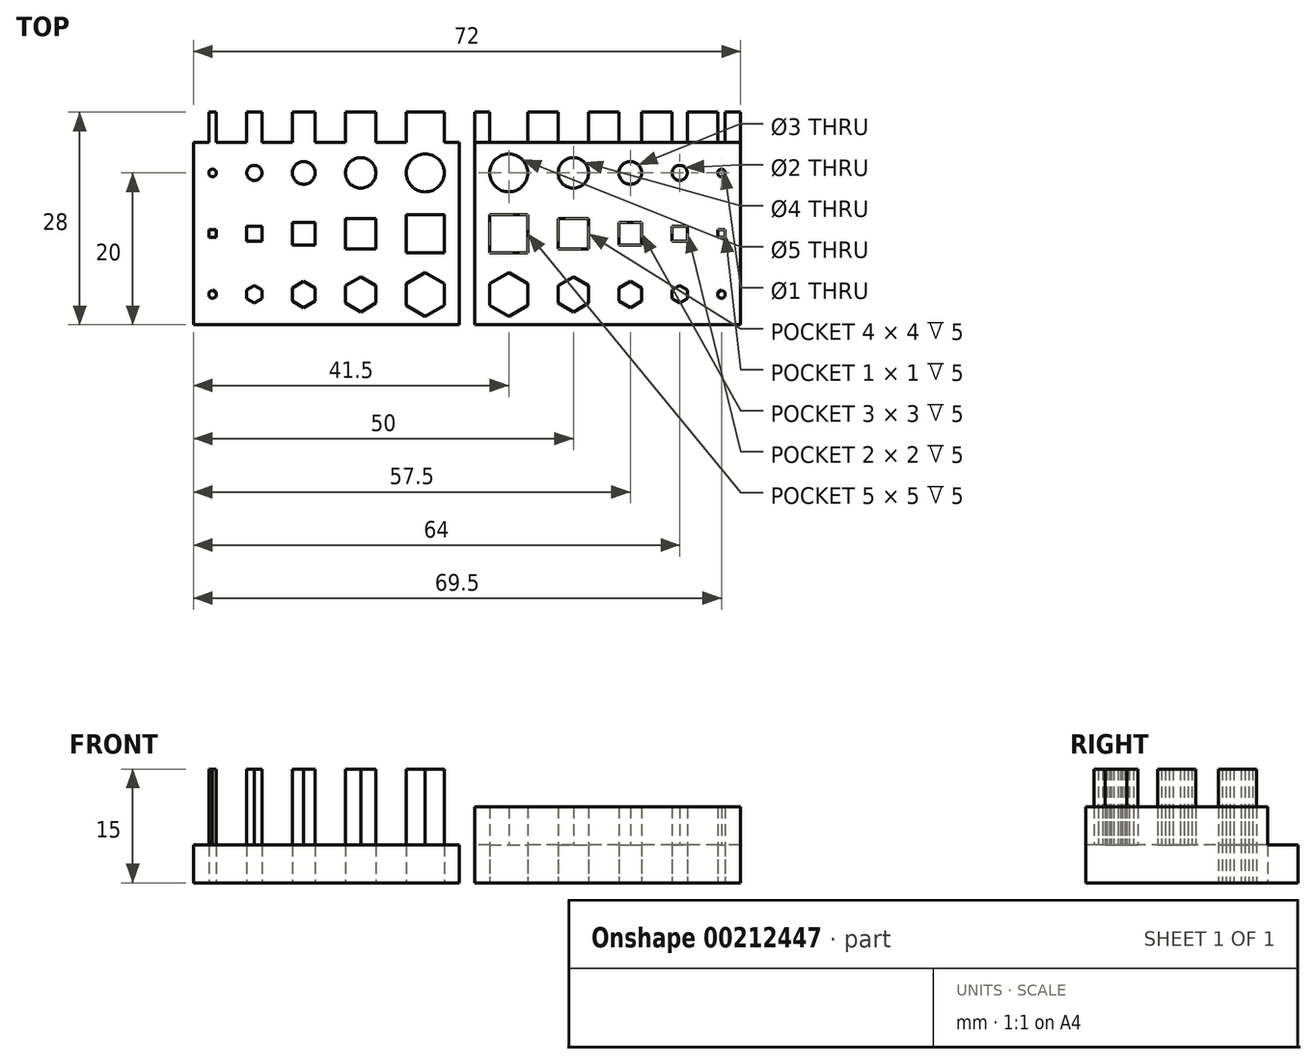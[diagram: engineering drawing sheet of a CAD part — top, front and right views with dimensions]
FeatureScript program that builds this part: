
annotation { "Feature Type Name" : "Feature", "Feature Type Description" : "" }
export const myFeature = defineFeature(function(context is Context, id is Id, definition is map)
    precondition{}
    {
        {
            var Q0;
            Q0=qCreatedBy(makeId("Top.planeOp"),FACE);
            var sketch = newSketch(context, id + "F0", { "sketchPlane" : qUnion([Q0])});
            skLineSegment(sketch, "E0.bottom", {"start": v(-36, 12) * mm, "end": v(36, 12) * mm});
            skLineSegment(sketch, "E0.top", {"start": v(-36, -12) * mm, "end": v(36, -12) * mm});
            skLineSegment(sketch, "E0.left", {"start": v(-36, 12) * mm, "end": v(-36, -12) * mm});
            skLineSegment(sketch, "E0.right", {"start": v(36, 12) * mm, "end": v(36, -12) * mm});
            skLineSegment(sketch, "E1", {"start": v(-36, 0) * mm, "end": v(36, 0) * mm, "construction": true});
            skLineSegment(sketch, "E2", {"start": v(-36, 8) * mm, "end": v(36, 8) * mm, "construction": true});
            skCircle(sketch, "E3", {"center": v(-33.5, 8) * mm, "radius": 0.5 * mm});
            skCircle(sketch, "E4", {"center": v(-28, 8) * mm, "radius": 1 * mm});
            skCircle(sketch, "E5", {"center": v(-21.5, 8) * mm, "radius": 1.5 * mm});
            skCircle(sketch, "E6", {"center": v(-14, 8) * mm, "radius": 2 * mm});
            skCircle(sketch, "E7", {"center": v(-5.5, 8) * mm, "radius": 2.5 * mm});
            skLineSegment(sketch, "E8.bottom", {"start": v(-34, 0.5) * mm, "end": v(-33, 0.5) * mm});
            skLineSegment(sketch, "E8.top", {"start": v(-34, -0.5) * mm, "end": v(-33, -0.5) * mm});
            skLineSegment(sketch, "E8.left", {"start": v(-34, 0.5) * mm, "end": v(-34, -0.5) * mm});
            skLineSegment(sketch, "E8.right", {"start": v(-33, 0.5) * mm, "end": v(-33, -0.5) * mm});
            skLineSegment(sketch, "E9.bottom", {"start": v(-23, 1.5) * mm, "end": v(-20, 1.5) * mm});
            skLineSegment(sketch, "E9.top", {"start": v(-23, -1.5) * mm, "end": v(-20, -1.5) * mm});
            skLineSegment(sketch, "E9.left", {"start": v(-23, 1.5) * mm, "end": v(-23, -1.5) * mm});
            skLineSegment(sketch, "E9.right", {"start": v(-20, 1.5) * mm, "end": v(-20, -1.5) * mm});
            skLineSegment(sketch, "E10.bottom", {"start": v(-16, 2) * mm, "end": v(-12, 2) * mm});
            skLineSegment(sketch, "E10.top", {"start": v(-16, -2) * mm, "end": v(-12, -2) * mm});
            skLineSegment(sketch, "E10.left", {"start": v(-16, 2) * mm, "end": v(-16, -2) * mm});
            skLineSegment(sketch, "E10.right", {"start": v(-12, 2) * mm, "end": v(-12, -2) * mm});
            skLineSegment(sketch, "E11.bottom", {"start": v(-8, 2.5) * mm, "end": v(-3, 2.5) * mm});
            skLineSegment(sketch, "E11.top", {"start": v(-8, -2.5) * mm, "end": v(-3, -2.5) * mm});
            skLineSegment(sketch, "E11.left", {"start": v(-8, 2.5) * mm, "end": v(-8, -2.5) * mm});
            skLineSegment(sketch, "E11.right", {"start": v(-3, 2.5) * mm, "end": v(-3, -2.5) * mm});
            skLineSegment(sketch, "E12", {"start": v(-8, 2.5) * mm, "end": v(-3, -2.5) * mm, "construction": true});
            skLineSegment(sketch, "E13", {"start": v(-16, 2) * mm, "end": v(-12, -2) * mm, "construction": true});
            skLineSegment(sketch, "E14", {"start": v(-23, 1.5) * mm, "end": v(-20, -1.5) * mm, "construction": true});
            skLineSegment(sketch, "E15", {"start": v(-34, 0.5) * mm, "end": v(-33, -0.5) * mm, "construction": true});
            skLineSegment(sketch, "E16.bottom", {"start": v(-29, 1) * mm, "end": v(-27, 1) * mm});
            skLineSegment(sketch, "E16.top", {"start": v(-29, -1) * mm, "end": v(-27, -1) * mm});
            skLineSegment(sketch, "E16.left", {"start": v(-29, 1) * mm, "end": v(-29, -1) * mm});
            skLineSegment(sketch, "E16.right", {"start": v(-27, 1) * mm, "end": v(-27, -1) * mm});
            skLineSegment(sketch, "E17.MirrorCS", {"start": v(-36, -8) * mm, "end": v(36, -8) * mm, "construction": true});
            skCircle(sketch, "E18.cCircle", {"center": v(-33.5, -8) * mm, "radius": 0.5 * mm, "construction": true});
            skLineSegment(sketch, "E18.0", {"start": v(-33.5, -7.42) * mm, "end": v(-33, -7.71) * mm});
            skLineSegment(sketch, "E18.1", {"start": v(-33, -7.71) * mm, "end": v(-33, -8.29) * mm});
            skLineSegment(sketch, "E18.2", {"start": v(-33, -8.29) * mm, "end": v(-33.5, -8.58) * mm});
            skLineSegment(sketch, "E18.3", {"start": v(-33.5, -8.58) * mm, "end": v(-34, -8.29) * mm});
            skLineSegment(sketch, "E18.4", {"start": v(-34, -8.29) * mm, "end": v(-34, -7.71) * mm});
            skLineSegment(sketch, "E18.5", {"start": v(-34, -7.71) * mm, "end": v(-33.5, -7.42) * mm});
            skPoint(sketch, "E18.0.midPoint", {"position": v(-33.25, -7.57) * mm});
            skCircle(sketch, "E19.cCircle", {"center": v(-21.5, -8) * mm, "radius": 1.5 * mm, "construction": true});
            skLineSegment(sketch, "E19.0", {"start": v(-21.5, -6.27) * mm, "end": v(-20, -7.13) * mm});
            skLineSegment(sketch, "E19.1", {"start": v(-20, -7.13) * mm, "end": v(-20, -8.87) * mm});
            skLineSegment(sketch, "E19.2", {"start": v(-20, -8.87) * mm, "end": v(-21.5, -9.73) * mm});
            skLineSegment(sketch, "E19.3", {"start": v(-21.5, -9.73) * mm, "end": v(-23, -8.87) * mm});
            skLineSegment(sketch, "E19.4", {"start": v(-23, -8.87) * mm, "end": v(-23, -7.13) * mm});
            skLineSegment(sketch, "E19.5", {"start": v(-23, -7.13) * mm, "end": v(-21.5, -6.27) * mm});
            skPoint(sketch, "E19.0.midPoint", {"position": v(-20.75, -6.7) * mm});
            skCircle(sketch, "E20.cCircle", {"center": v(-14, -8) * mm, "radius": 2 * mm, "construction": true});
            skLineSegment(sketch, "E20.0", {"start": v(-14, -5.7) * mm, "end": v(-12, -6.85) * mm});
            skLineSegment(sketch, "E20.1", {"start": v(-12, -6.85) * mm, "end": v(-12, -9.15) * mm});
            skLineSegment(sketch, "E20.2", {"start": v(-12, -9.15) * mm, "end": v(-14, -10.3) * mm});
            skLineSegment(sketch, "E20.3", {"start": v(-14, -10.3) * mm, "end": v(-16, -9.15) * mm});
            skLineSegment(sketch, "E20.4", {"start": v(-16, -9.15) * mm, "end": v(-16, -6.85) * mm});
            skLineSegment(sketch, "E20.5", {"start": v(-16, -6.85) * mm, "end": v(-14, -5.7) * mm});
            skPoint(sketch, "E20.0.midPoint", {"position": v(-13, -6.27) * mm});
            skCircle(sketch, "E21.cCircle", {"center": v(-5.5, -8) * mm, "radius": 2.5 * mm, "construction": true});
            skLineSegment(sketch, "E21.0", {"start": v(-8, -6.56) * mm, "end": v(-5.5, -5.11) * mm});
            skLineSegment(sketch, "E21.1", {"start": v(-5.5, -5.11) * mm, "end": v(-3, -6.56) * mm});
            skLineSegment(sketch, "E21.2", {"start": v(-3, -6.56) * mm, "end": v(-3, -9.44) * mm});
            skLineSegment(sketch, "E21.3", {"start": v(-3, -9.44) * mm, "end": v(-5.5, -10.89) * mm});
            skLineSegment(sketch, "E21.4", {"start": v(-5.5, -10.89) * mm, "end": v(-8, -9.44) * mm});
            skLineSegment(sketch, "E21.5", {"start": v(-8, -9.44) * mm, "end": v(-8, -6.56) * mm});
            skPoint(sketch, "E21.0.midPoint", {"position": v(-6.75, -5.83) * mm});
            skCircle(sketch, "E22.cCircle", {"center": v(-28, -8) * mm, "radius": 1 * mm, "construction": true});
            skLineSegment(sketch, "E22.0", {"start": v(-28, -6.85) * mm, "end": v(-27, -7.42) * mm});
            skLineSegment(sketch, "E22.1", {"start": v(-27, -7.42) * mm, "end": v(-27, -8.58) * mm});
            skLineSegment(sketch, "E22.2", {"start": v(-27, -8.58) * mm, "end": v(-28, -9.15) * mm});
            skLineSegment(sketch, "E22.3", {"start": v(-28, -9.15) * mm, "end": v(-29, -8.58) * mm});
            skLineSegment(sketch, "E22.4", {"start": v(-29, -8.58) * mm, "end": v(-29, -7.42) * mm});
            skLineSegment(sketch, "E22.5", {"start": v(-29, -7.42) * mm, "end": v(-28, -6.85) * mm});
            skPoint(sketch, "E22.0.midPoint", {"position": v(-27.5, -7.13) * mm});
            skLineSegment(sketch, "E23.MirrorCS", {"start": v(33, -7.71) * mm, "end": v(33, -8.29) * mm});
            skLineSegment(sketch, "E24.MirrorCS", {"start": v(33.5, -7.42) * mm, "end": v(33, -7.71) * mm});
            skLineSegment(sketch, "E25.MirrorCS", {"start": v(33.5, -8.58) * mm, "end": v(34, -8.29) * mm});
            skLineSegment(sketch, "E26.MirrorCS", {"start": v(33, -8.29) * mm, "end": v(33.5, -8.58) * mm});
            skLineSegment(sketch, "E27.MirrorCS", {"start": v(27, -8.58) * mm, "end": v(28, -9.15) * mm});
            skLineSegment(sketch, "E28.MirrorCS", {"start": v(34, -7.71) * mm, "end": v(33.5, -7.42) * mm});
            skLineSegment(sketch, "E29.MirrorCS", {"start": v(34, 0.5) * mm, "end": v(33, -0.5) * mm, "construction": true});
            skCircle(sketch, "E30.MirrorC", {"center": v(33.5, -8) * mm, "radius": 0.5 * mm, "construction": true});
            skLineSegment(sketch, "E31.MirrorCS", {"start": v(34, -8.29) * mm, "end": v(34, -7.71) * mm});
            skLineSegment(sketch, "E32.MirrorCS", {"start": v(28, -9.15) * mm, "end": v(29, -8.58) * mm});
            skLineSegment(sketch, "E33.MirrorCS", {"start": v(34, 0.5) * mm, "end": v(33, 0.5) * mm});
            skLineSegment(sketch, "E34.MirrorCS", {"start": v(20, -7.13) * mm, "end": v(20, -8.87) * mm});
            skLineSegment(sketch, "E35.MirrorCS", {"start": v(21.5, -6.27) * mm, "end": v(20, -7.13) * mm});
            skLineSegment(sketch, "E36.MirrorCS", {"start": v(20, -8.87) * mm, "end": v(21.5, -9.73) * mm});
            skLineSegment(sketch, "E37.MirrorCS", {"start": v(34, 0.5) * mm, "end": v(34, -0.5) * mm});
            skLineSegment(sketch, "E38.MirrorCS", {"start": v(21.5, -9.73) * mm, "end": v(23, -8.87) * mm});
            skLineSegment(sketch, "E39.MirrorCS", {"start": v(29, -7.42) * mm, "end": v(28, -6.85) * mm});
            skCircle(sketch, "E40.MirrorC", {"center": v(21.5, -8) * mm, "radius": 1.5 * mm, "construction": true});
            skLineSegment(sketch, "E41.MirrorCS", {"start": v(28, -6.85) * mm, "end": v(27, -7.42) * mm});
            skLineSegment(sketch, "E42.MirrorCS", {"start": v(23, -7.13) * mm, "end": v(21.5, -6.27) * mm});
            skLineSegment(sketch, "E43.MirrorCS", {"start": v(33, 0.5) * mm, "end": v(33, -0.5) * mm});
            skLineSegment(sketch, "E44.MirrorCS", {"start": v(29, -8.58) * mm, "end": v(29, -7.42) * mm});
            skLineSegment(sketch, "E45.MirrorCS", {"start": v(23, -8.87) * mm, "end": v(23, -7.13) * mm});
            skLineSegment(sketch, "E46.MirrorCS", {"start": v(34, -0.5) * mm, "end": v(33, -0.5) * mm});
            skCircle(sketch, "E47.MirrorC", {"center": v(28, -8) * mm, "radius": 1 * mm, "construction": true});
            skLineSegment(sketch, "E48.MirrorCS", {"start": v(27, -7.42) * mm, "end": v(27, -8.58) * mm});
            skLineSegment(sketch, "E49.MirrorCS", {"start": v(16, -9.15) * mm, "end": v(16, -6.85) * mm});
            skCircle(sketch, "E50.MirrorC", {"center": v(33.5, 8) * mm, "radius": 0.5 * mm});
            skLineSegment(sketch, "E51.MirrorCS", {"start": v(8, -6.56) * mm, "end": v(5.5, -5.11) * mm});
            skLineSegment(sketch, "E52.MirrorCS", {"start": v(3, -9.44) * mm, "end": v(5.5, -10.89) * mm});
            skLineSegment(sketch, "E53.MirrorCS", {"start": v(3, -6.56) * mm, "end": v(3, -9.44) * mm});
            skLineSegment(sketch, "E54.MirrorCS", {"start": v(14, -10.3) * mm, "end": v(16, -9.15) * mm});
            skLineSegment(sketch, "E55.MirrorCS", {"start": v(16, -6.85) * mm, "end": v(14, -5.7) * mm});
            skLineSegment(sketch, "E56.MirrorCS", {"start": v(12, -6.85) * mm, "end": v(12, -9.15) * mm});
            skLineSegment(sketch, "E57.MirrorCS", {"start": v(14, -5.7) * mm, "end": v(12, -6.85) * mm});
            skPoint(sketch, "E58.MirrorP", {"position": v(13, -6.27) * mm});
            skLineSegment(sketch, "E59.MirrorCS", {"start": v(20, 1.5) * mm, "end": v(20, -1.5) * mm});
            skPoint(sketch, "E60.MirrorP", {"position": v(27.5, -7.13) * mm});
            skLineSegment(sketch, "E61.MirrorCS", {"start": v(16, -2) * mm, "end": v(12, -2) * mm});
            skLineSegment(sketch, "E62.MirrorCS", {"start": v(8, 2.5) * mm, "end": v(3, -2.5) * mm, "construction": true});
            skLineSegment(sketch, "E63.MirrorCS", {"start": v(8, 2.5) * mm, "end": v(3, 2.5) * mm});
            skCircle(sketch, "E64.MirrorC", {"center": v(21.5, 8) * mm, "radius": 1.5 * mm});
            skCircle(sketch, "E65.MirrorC", {"center": v(28, 8) * mm, "radius": 1 * mm});
            skLineSegment(sketch, "E66.MirrorCS", {"start": v(16, 2) * mm, "end": v(16, -2) * mm});
            skLineSegment(sketch, "E67.MirrorCS", {"start": v(16, 2) * mm, "end": v(12, -2) * mm, "construction": true});
            skPoint(sketch, "E68.MirrorP", {"position": v(33.25, -7.57) * mm});
            skCircle(sketch, "E69.MirrorC", {"center": v(14, 8) * mm, "radius": 2 * mm});
            skCircle(sketch, "E70.MirrorC", {"center": v(5.5, 8) * mm, "radius": 2.5 * mm});
            skLineSegment(sketch, "E71.MirrorCS", {"start": v(23, -1.5) * mm, "end": v(20, -1.5) * mm});
            skLineSegment(sketch, "E72.MirrorCS", {"start": v(12, -9.15) * mm, "end": v(14, -10.3) * mm});
            skPoint(sketch, "E73.MirrorP", {"position": v(20.75, -6.7) * mm});
            skLineSegment(sketch, "E74.MirrorCS", {"start": v(29, 1) * mm, "end": v(27, 1) * mm});
            skCircle(sketch, "E75.MirrorC", {"center": v(14, -8) * mm, "radius": 2 * mm, "construction": true});
            skLineSegment(sketch, "E76.MirrorCS", {"start": v(8, -9.44) * mm, "end": v(8, -6.56) * mm});
            skLineSegment(sketch, "E77.MirrorCS", {"start": v(12, 2) * mm, "end": v(12, -2) * mm});
            skLineSegment(sketch, "E78.MirrorCS", {"start": v(23, 1.5) * mm, "end": v(20, 1.5) * mm});
            skCircle(sketch, "E79.MirrorC", {"center": v(5.5, -8) * mm, "radius": 2.5 * mm, "construction": true});
            skLineSegment(sketch, "E80.MirrorCS", {"start": v(23, 1.5) * mm, "end": v(20, -1.5) * mm, "construction": true});
            skLineSegment(sketch, "E81.MirrorCS", {"start": v(29, -1) * mm, "end": v(27, -1) * mm});
            skLineSegment(sketch, "E82.MirrorCS", {"start": v(3, 2.5) * mm, "end": v(3, -2.5) * mm});
            skLineSegment(sketch, "E83.MirrorCS", {"start": v(27, 1) * mm, "end": v(27, -1) * mm});
            skLineSegment(sketch, "E84.MirrorCS", {"start": v(23, 1.5) * mm, "end": v(23, -1.5) * mm});
            skPoint(sketch, "E85.MirrorP", {"position": v(6.75, -5.83) * mm});
            skLineSegment(sketch, "E86.MirrorCS", {"start": v(8, 2.5) * mm, "end": v(8, -2.5) * mm});
            skLineSegment(sketch, "E87.MirrorCS", {"start": v(16, 2) * mm, "end": v(12, 2) * mm});
            skLineSegment(sketch, "E88.MirrorCS", {"start": v(5.5, -5.11) * mm, "end": v(3, -6.56) * mm});
            skLineSegment(sketch, "E89.MirrorCS", {"start": v(29, 1) * mm, "end": v(29, -1) * mm});
            skLineSegment(sketch, "E90.MirrorCS", {"start": v(5.5, -10.89) * mm, "end": v(8, -9.44) * mm});
            skLineSegment(sketch, "E91.MirrorCS", {"start": v(8, -2.5) * mm, "end": v(3, -2.5) * mm});
            skLineSegment(sketch, "E92.bottom", {"start": v(-34, 16) * mm, "end": v(-33, 16) * mm});
            skLineSegment(sketch, "E92.top", {"start": v(-34, 12) * mm, "end": v(-33, 12) * mm});
            skLineSegment(sketch, "E92.left", {"start": v(-34, 16) * mm, "end": v(-34, 12) * mm});
            skLineSegment(sketch, "E92.right", {"start": v(-33, 16) * mm, "end": v(-33, 12) * mm});
            skLineSegment(sketch, "E93.bottom", {"start": v(-29, 16) * mm, "end": v(-27, 16) * mm});
            skLineSegment(sketch, "E93.top", {"start": v(-29, 12) * mm, "end": v(-27, 12) * mm});
            skLineSegment(sketch, "E93.left", {"start": v(-29, 16) * mm, "end": v(-29, 12) * mm});
            skLineSegment(sketch, "E93.right", {"start": v(-27, 16) * mm, "end": v(-27, 12) * mm});
            skLineSegment(sketch, "E94.bottom", {"start": v(-23, 16) * mm, "end": v(-20, 16) * mm});
            skLineSegment(sketch, "E94.top", {"start": v(-23, 12) * mm, "end": v(-20, 12) * mm});
            skLineSegment(sketch, "E94.left", {"start": v(-23, 16) * mm, "end": v(-23, 12) * mm});
            skLineSegment(sketch, "E94.right", {"start": v(-20, 16) * mm, "end": v(-20, 12) * mm});
            skLineSegment(sketch, "E95.bottom", {"start": v(-16, 16) * mm, "end": v(-12, 16) * mm});
            skLineSegment(sketch, "E95.top", {"start": v(-16, 12) * mm, "end": v(-12, 12) * mm});
            skLineSegment(sketch, "E95.left", {"start": v(-16, 16) * mm, "end": v(-16, 12) * mm});
            skLineSegment(sketch, "E95.right", {"start": v(-12, 16) * mm, "end": v(-12, 12) * mm});
            skLineSegment(sketch, "E96.bottom", {"start": v(-8, 16) * mm, "end": v(-3, 16) * mm});
            skLineSegment(sketch, "E96.top", {"start": v(-8, 12) * mm, "end": v(-3, 12) * mm});
            skLineSegment(sketch, "E96.left", {"start": v(-8, 16) * mm, "end": v(-8, 12) * mm});
            skLineSegment(sketch, "E96.right", {"start": v(-3, 16) * mm, "end": v(-3, 12) * mm});
            skLineSegment(sketch, "E97.MirrorCS", {"start": v(34, 16) * mm, "end": v(33, 16) * mm});
            skLineSegment(sketch, "E98.MirrorCS", {"start": v(34, 12) * mm, "end": v(33, 12) * mm});
            skLineSegment(sketch, "E99.MirrorCS", {"start": v(29, 12) * mm, "end": v(27, 12) * mm});
            skLineSegment(sketch, "E100.MirrorCS", {"start": v(29, 16) * mm, "end": v(27, 16) * mm});
            skLineSegment(sketch, "E101.MirrorCS", {"start": v(16, 16) * mm, "end": v(16, 12) * mm});
            skLineSegment(sketch, "E102.MirrorCS", {"start": v(8, 16) * mm, "end": v(8, 12) * mm});
            skLineSegment(sketch, "E103.MirrorCS", {"start": v(20, 16) * mm, "end": v(20, 12) * mm});
            skLineSegment(sketch, "E104.MirrorCS", {"start": v(16, 16) * mm, "end": v(12, 16) * mm});
            skLineSegment(sketch, "E105.MirrorCS", {"start": v(23, 16) * mm, "end": v(23, 12) * mm});
            skLineSegment(sketch, "E106.MirrorCS", {"start": v(16, 12) * mm, "end": v(12, 12) * mm});
            skLineSegment(sketch, "E107.MirrorCS", {"start": v(12, 16) * mm, "end": v(12, 12) * mm});
            skLineSegment(sketch, "E108.MirrorCS", {"start": v(8, 16) * mm, "end": v(3, 16) * mm});
            skLineSegment(sketch, "E109.MirrorCS", {"start": v(8, 12) * mm, "end": v(3, 12) * mm});
            skLineSegment(sketch, "E110.MirrorCS", {"start": v(34, 16) * mm, "end": v(34, 12) * mm});
            skLineSegment(sketch, "E111.MirrorCS", {"start": v(23, 16) * mm, "end": v(20, 16) * mm});
            skLineSegment(sketch, "E112.MirrorCS", {"start": v(23, 12) * mm, "end": v(20, 12) * mm});
            skLineSegment(sketch, "E113.MirrorCS", {"start": v(33, 16) * mm, "end": v(33, 12) * mm});
            skLineSegment(sketch, "E114.MirrorCS", {"start": v(29, 16) * mm, "end": v(29, 12) * mm});
            skLineSegment(sketch, "E115.MirrorCS", {"start": v(3, 16) * mm, "end": v(3, 12) * mm});
            skLineSegment(sketch, "E116.MirrorCS", {"start": v(27, 16) * mm, "end": v(27, 12) * mm});
            skLineSegment(sketch, "E117.bottom", {"start": v(36, 12) * mm, "end": v(0, 12) * mm});
            skLineSegment(sketch, "E117.top", {"start": v(36, 16) * mm, "end": v(0, 16) * mm});
            skLineSegment(sketch, "E117.left", {"start": v(36, 12) * mm, "end": v(36, 16) * mm});
            skLineSegment(sketch, "E117.right", {"start": v(0, 12) * mm, "end": v(0, 16) * mm});
            skLineSegment(sketch, "E118.1.18", {"start": v(36, -12.69) * mm, "end": v(-36, -12.69) * mm});
            skPoint(sketch, "E118.center", {"position": v(0, -0.34) * mm});
            skLineSegment(sketch, "E119", {"start": v(0, 12) * mm, "end": v(0, -12.69) * mm});
            skLineSegment(sketch, "E120.bottom", {"start": v(-1, 18.91) * mm, "end": v(1, 18.91) * mm});
            skLineSegment(sketch, "E120.top", {"start": v(-1, -18.8) * mm, "end": v(1, -18.8) * mm});
            skLineSegment(sketch, "E120.left", {"start": v(-1, 18.91) * mm, "end": v(-1, -18.8) * mm});
            skLineSegment(sketch, "E120.right", {"start": v(1, 18.91) * mm, "end": v(1, -18.8) * mm});
            skSolve(sketch);
        }
        {
            var Q0;
            Q0=makeQuery(id+"F0.imprint","IMPRINT",FACE,{"disambiguationData":[TD([[makeQuery(id+"F0.imprint","IMPRINT",EDGE,{"derivedFrom":sQuery(id+"F0.wireOp",EDGE,"E96.bottom")}),-1.0]])]});
            var Q1;
            Q1=makeQuery(id+"F0.imprint","IMPRINT",FACE,{"disambiguationData":[TD([[makeQuery(id+"F0.imprint","IMPRINT",EDGE,{"derivedFrom":sQuery(id+"F0.wireOp",EDGE,"E95.bottom")}),-1.0]])]});
            var Q2;
            Q2=makeQuery(id+"F0.imprint","IMPRINT",FACE,{"disambiguationData":[TD([[makeQuery(id+"F0.imprint","IMPRINT",EDGE,{"derivedFrom":sQuery(id+"F0.wireOp",EDGE,"E93.bottom")}),-1.0]])]});
            var Q3;
            Q3=makeQuery(id+"F0.imprint","IMPRINT",FACE,{"disambiguationData":[TD([[makeQuery(id+"F0.imprint","IMPRINT",EDGE,{"derivedFrom":sQuery(id+"F0.wireOp",EDGE,"E94.bottom")}),-1.0]])]});
            var Q4;
            Q4=makeQuery(id+"F0.imprint","IMPRINT",FACE,{"disambiguationData":[TD([[makeQuery(id+"F0.imprint","IMPRINT",EDGE,{"derivedFrom":sQuery(id+"F0.wireOp",EDGE,"E92.bottom")}),-1.0]])]});
            var Q5;
            {var subQ4=sQuery(id+"F0.wireOp",EDGE,"E0.left");Q5=makeQuery(id+"F0.imprint","IMPRINT",FACE,{"disambiguationData":[TD([[makeQuery(id+"F0.imprint","IMPRINT",EDGE,{"derivedFrom":subQ4}),1.0]])]});}
            var Q6;
            Q6=makeQuery(id+"F0.imprint","IMPRINT",FACE,{"disambiguationData":[TD([[makeQuery(id+"F0.imprint","IMPRINT",EDGE,{"derivedFrom":sQuery(id+"F0.wireOp",EDGE,"E20.0")}),-1.0]])]});
            var Q7;
            Q7=makeQuery(id+"F0.imprint","IMPRINT",FACE,{"disambiguationData":[TD([[makeQuery(id+"F0.imprint","IMPRINT",EDGE,{"derivedFrom":sQuery(id+"F0.wireOp",EDGE,"E19.0")}),-1.0]])]});
            var Q8;
            Q8=makeQuery(id+"F0.imprint","IMPRINT",FACE,{"disambiguationData":[TD([[makeQuery(id+"F0.imprint","IMPRINT",EDGE,{"derivedFrom":sQuery(id+"F0.wireOp",EDGE,"E11.bottom")}),-1.0]])]});
            var Q9;
            Q9=makeQuery(id+"F0.imprint","IMPRINT",FACE,{"disambiguationData":[TD([[makeQuery(id+"F0.imprint","IMPRINT",EDGE,{"derivedFrom":sQuery(id+"F0.wireOp",EDGE,"E16.bottom")}),-1.0]])]});
            var Q10;
            Q10=makeQuery(id+"F0.imprint","IMPRINT",FACE,{"disambiguationData":[TD([[makeQuery(id+"F0.imprint","IMPRINT",EDGE,{"derivedFrom":sQuery(id+"F0.wireOp",EDGE,"E10.bottom")}),-1.0]])]});
            var Q11;
            Q11=makeQuery(id+"F0.imprint","IMPRINT",FACE,{"disambiguationData":[TD([[makeQuery(id+"F0.imprint","IMPRINT",EDGE,{"derivedFrom":sQuery(id+"F0.wireOp",EDGE,"E9.bottom")}),-1.0]])]});
            var Q12;
            Q12=makeQuery(id+"F0.imprint","IMPRINT",FACE,{"disambiguationData":[TD([[makeQuery(id+"F0.imprint","IMPRINT",EDGE,{"derivedFrom":sQuery(id+"F0.wireOp",EDGE,"E4")}),1.0]])]});
            var Q13;
            Q13=makeQuery(id+"F0.imprint","IMPRINT",FACE,{"disambiguationData":[TD([[makeQuery(id+"F0.imprint","IMPRINT",EDGE,{"derivedFrom":sQuery(id+"F0.wireOp",EDGE,"E22.0")}),-1.0]])]});
            var Q14;
            Q14=makeQuery(id+"F0.imprint","IMPRINT",FACE,{"disambiguationData":[TD([[makeQuery(id+"F0.imprint","IMPRINT",EDGE,{"derivedFrom":sQuery(id+"F0.wireOp",EDGE,"E3")}),1.0]])]});
            var Q15;
            Q15=makeQuery(id+"F0.imprint","IMPRINT",FACE,{"disambiguationData":[TD([[makeQuery(id+"F0.imprint","IMPRINT",EDGE,{"derivedFrom":sQuery(id+"F0.wireOp",EDGE,"E18.0")}),-1.0]])]});
            var Q16;
            Q16=makeQuery(id+"F0.imprint","IMPRINT",FACE,{"disambiguationData":[TD([[makeQuery(id+"F0.imprint","IMPRINT",EDGE,{"derivedFrom":sQuery(id+"F0.wireOp",EDGE,"E8.bottom")}),-1.0]])]});
            var Q17;
            Q17=makeQuery(id+"F0.imprint","IMPRINT",FACE,{"disambiguationData":[TD([[makeQuery(id+"F0.imprint","IMPRINT",EDGE,{"derivedFrom":sQuery(id+"F0.wireOp",EDGE,"E7")}),1.0]])]});
            var Q18;
            Q18=makeQuery(id+"F0.imprint","IMPRINT",FACE,{"disambiguationData":[TD([[makeQuery(id+"F0.imprint","IMPRINT",EDGE,{"derivedFrom":sQuery(id+"F0.wireOp",EDGE,"E6")}),1.0]])]});
            var Q19;
            Q19=makeQuery(id+"F0.imprint","IMPRINT",FACE,{"disambiguationData":[TD([[makeQuery(id+"F0.imprint","IMPRINT",EDGE,{"derivedFrom":sQuery(id+"F0.wireOp",EDGE,"E5")}),1.0]])]});
            var Q20;
            Q20=makeQuery(id+"F0.imprint","IMPRINT",FACE,{"disambiguationData":[TD([[makeQuery(id+"F0.imprint","IMPRINT",EDGE,{"derivedFrom":sQuery(id+"F0.wireOp",EDGE,"E21.0")}),-1.0]])]});
            var Q21;
            Q21=makeQuery(id+"F0.imprint","IMPRINT",FACE,{"disambiguationData":[TD([[makeQuery(id+"F0.imprint","IMPRINT",EDGE,{"derivedFrom":sQuery(id+"F0.wireOp",EDGE,"E51.MirrorCS")}),1.0]])]});
            var Q22;
            Q22=makeQuery(id+"F0.imprint","IMPRINT",FACE,{"disambiguationData":[TD([[makeQuery(id+"F0.imprint","IMPRINT",EDGE,{"derivedFrom":sQuery(id+"F0.wireOp",EDGE,"E63.MirrorCS")}),1.0]])]});
            var Q23;
            Q23=makeQuery(id+"F0.imprint","IMPRINT",FACE,{"disambiguationData":[TD([[makeQuery(id+"F0.imprint","IMPRINT",EDGE,{"derivedFrom":sQuery(id+"F0.wireOp",EDGE,"E70.MirrorC")}),-1.0]])]});
            var Q24;
            {var subQ0=sQuery(id+"F0.wireOp",EDGE,"E0.right");Q24=makeQuery(id+"F0.imprint","IMPRINT",FACE,{"disambiguationData":[TD([[makeQuery(id+"F0.imprint","IMPRINT",EDGE,{"derivedFrom":subQ0}),-1.0]])]});}
            var Q25;
            Q25=makeQuery(id+"F0.imprint","IMPRINT",FACE,{"disambiguationData":[TD([[makeQuery(id+"F0.imprint","IMPRINT",EDGE,{"derivedFrom":sQuery(id+"F0.wireOp",EDGE,"E59.MirrorCS")}),1.0]])]});
            var Q26;
            {var subQ0=sQuery(id+"F0.wireOp",EDGE,"E102.MirrorCS");Q26=makeQuery(id+"F0.imprint","IMPRINT",FACE,{"disambiguationData":[TD([[makeQuery(id+"F0.imprint","IMPRINT",EDGE,{"derivedFrom":subQ0}),1.0]])]});}
            var Q27;
            Q27=makeQuery(id+"F0.imprint","IMPRINT",FACE,{"disambiguationData":[TD([[makeQuery(id+"F0.imprint","IMPRINT",EDGE,{"derivedFrom":sQuery(id+"F0.wireOp",EDGE,"E61.MirrorCS")}),-1.0]])]});
            var Q28;
            {var subQ0=sQuery(id+"F0.wireOp",EDGE,"E105.MirrorCS");Q28=makeQuery(id+"F0.imprint","IMPRINT",FACE,{"disambiguationData":[TD([[makeQuery(id+"F0.imprint","IMPRINT",EDGE,{"derivedFrom":subQ0}),1.0]])]});}
            var Q29;
            Q29=makeQuery(id+"F0.imprint","IMPRINT",FACE,{"disambiguationData":[TD([[makeQuery(id+"F0.imprint","IMPRINT",EDGE,{"derivedFrom":sQuery(id+"F0.wireOp",EDGE,"E65.MirrorC")}),-1.0]])]});
            var Q30;
            Q30=makeQuery(id+"F0.imprint","IMPRINT",FACE,{"disambiguationData":[TD([[makeQuery(id+"F0.imprint","IMPRINT",EDGE,{"derivedFrom":sQuery(id+"F0.wireOp",EDGE,"E74.MirrorCS")}),1.0]])]});
            var Q31;
            Q31=makeQuery(id+"F0.imprint","IMPRINT",FACE,{"disambiguationData":[TD([[makeQuery(id+"F0.imprint","IMPRINT",EDGE,{"derivedFrom":sQuery(id+"F0.wireOp",EDGE,"E34.MirrorCS")}),1.0]])]});
            var Q32;
            {var subQ0=sQuery(id+"F0.wireOp",EDGE,"E113.MirrorCS");Q32=makeQuery(id+"F0.imprint","IMPRINT",FACE,{"disambiguationData":[TD([[makeQuery(id+"F0.imprint","IMPRINT",EDGE,{"derivedFrom":subQ0}),-1.0]])]});}
            var Q33;
            Q33=makeQuery(id+"F0.imprint","IMPRINT",FACE,{"disambiguationData":[TD([[makeQuery(id+"F0.imprint","IMPRINT",EDGE,{"derivedFrom":sQuery(id+"F0.wireOp",EDGE,"E49.MirrorCS")}),1.0]])]});
            var Q34;
            {var subQ0=sQuery(id+"F0.wireOp",EDGE,"E110.MirrorCS");Q34=makeQuery(id+"F0.imprint","IMPRINT",FACE,{"disambiguationData":[TD([[makeQuery(id+"F0.imprint","IMPRINT",EDGE,{"derivedFrom":subQ0}),1.0]])]});}
            var Q35;
            {var subQ0=sQuery(id+"F0.wireOp",EDGE,"E115.MirrorCS");Q35=makeQuery(id+"F0.imprint","IMPRINT",FACE,{"disambiguationData":[TD([[makeQuery(id+"F0.imprint","IMPRINT",EDGE,{"derivedFrom":subQ0}),-1.0]])]});}
            var Q36;
            Q36=makeQuery(id+"F0.imprint","IMPRINT",FACE,{"disambiguationData":[TD([[makeQuery(id+"F0.imprint","IMPRINT",EDGE,{"derivedFrom":sQuery(id+"F0.wireOp",EDGE,"E69.MirrorC")}),-1.0]])]});
            var Q37;
            {var subQ0=sQuery(id+"F0.wireOp",EDGE,"E101.MirrorCS");Q37=makeQuery(id+"F0.imprint","IMPRINT",FACE,{"disambiguationData":[TD([[makeQuery(id+"F0.imprint","IMPRINT",EDGE,{"derivedFrom":subQ0}),1.0]])]});}
            var Q38;
            Q38=makeQuery(id+"F0.imprint","IMPRINT",FACE,{"disambiguationData":[TD([[makeQuery(id+"F0.imprint","IMPRINT",EDGE,{"derivedFrom":sQuery(id+"F0.wireOp",EDGE,"E64.MirrorC")}),-1.0]])]});
            var Q39;
            Q39=makeQuery(id+"F0.imprint","IMPRINT",FACE,{"disambiguationData":[TD([[makeQuery(id+"F0.imprint","IMPRINT",EDGE,{"derivedFrom":sQuery(id+"F0.wireOp",EDGE,"E27.MirrorCS")}),1.0]])]});
            var Q40;
            Q40=makeQuery(id+"F0.imprint","IMPRINT",FACE,{"disambiguationData":[TD([[makeQuery(id+"F0.imprint","IMPRINT",EDGE,{"derivedFrom":sQuery(id+"F0.wireOp",EDGE,"E50.MirrorC")}),-1.0]])]});
            var Q41;
            Q41=makeQuery(id+"F0.imprint","IMPRINT",FACE,{"disambiguationData":[TD([[makeQuery(id+"F0.imprint","IMPRINT",EDGE,{"derivedFrom":sQuery(id+"F0.wireOp",EDGE,"E23.MirrorCS")}),1.0]])]});
            var Q42;
            Q42=makeQuery(id+"F0.imprint","IMPRINT",FACE,{"disambiguationData":[TD([[makeQuery(id+"F0.imprint","IMPRINT",EDGE,{"derivedFrom":sQuery(id+"F0.wireOp",EDGE,"E33.MirrorCS")}),1.0]])]});
            extrude(context, id + "F1", {"entities" : qUnion([Q0, Q1, Q2, Q3, Q4, Q5, Q6, Q7, Q8, Q9, Q10, Q11, Q12, Q13, Q14, Q15, Q16, Q17, Q18, Q19, Q20, Q21, Q22, Q23, Q24, Q25, Q26, Q27, Q28, Q29, Q30, Q31, Q32, Q33, Q34, Q35, Q36, Q37, Q38, Q39, Q40, Q41, Q42]), "depth" : 5 * mm});
        }
        {
            var Q0;
            {var subQ0=sQuery(id+"F0.wireOp",EDGE,"E0.right");Q0=makeQuery(id+"F0.imprint","IMPRINT",FACE,{"disambiguationData":[TD([[makeQuery(id+"F0.imprint","IMPRINT",EDGE,{"derivedFrom":subQ0}),-1.0]])]});}
            extrude(context, id + "F2", {"entities" : qUnion([Q0]), "operationType" : NewBodyOperationType.ADD, "depth" : 10 * mm});
        }
        {
            var Q0;
            Q0=makeQuery(id+"F0.imprint","IMPRINT",FACE,{"disambiguationData":[TD([[makeQuery(id+"F0.imprint","IMPRINT",EDGE,{"derivedFrom":sQuery(id+"F0.wireOp",EDGE,"E9.bottom")}),-1.0]])]});
            var Q1;
            Q1=makeQuery(id+"F0.imprint","IMPRINT",FACE,{"disambiguationData":[TD([[makeQuery(id+"F0.imprint","IMPRINT",EDGE,{"derivedFrom":sQuery(id+"F0.wireOp",EDGE,"E4")}),1.0]])]});
            var Q2;
            Q2=makeQuery(id+"F0.imprint","IMPRINT",FACE,{"disambiguationData":[TD([[makeQuery(id+"F0.imprint","IMPRINT",EDGE,{"derivedFrom":sQuery(id+"F0.wireOp",EDGE,"E5")}),1.0]])]});
            var Q3;
            Q3=makeQuery(id+"F0.imprint","IMPRINT",FACE,{"disambiguationData":[TD([[makeQuery(id+"F0.imprint","IMPRINT",EDGE,{"derivedFrom":sQuery(id+"F0.wireOp",EDGE,"E21.0")}),-1.0]])]});
            var Q4;
            Q4=makeQuery(id+"F0.imprint","IMPRINT",FACE,{"disambiguationData":[TD([[makeQuery(id+"F0.imprint","IMPRINT",EDGE,{"derivedFrom":sQuery(id+"F0.wireOp",EDGE,"E22.0")}),-1.0]])]});
            var Q5;
            Q5=makeQuery(id+"F0.imprint","IMPRINT",FACE,{"disambiguationData":[TD([[makeQuery(id+"F0.imprint","IMPRINT",EDGE,{"derivedFrom":sQuery(id+"F0.wireOp",EDGE,"E11.bottom")}),-1.0]])]});
            var Q6;
            Q6=makeQuery(id+"F0.imprint","IMPRINT",FACE,{"disambiguationData":[TD([[makeQuery(id+"F0.imprint","IMPRINT",EDGE,{"derivedFrom":sQuery(id+"F0.wireOp",EDGE,"E6")}),1.0]])]});
            var Q7;
            Q7=makeQuery(id+"F0.imprint","IMPRINT",FACE,{"disambiguationData":[TD([[makeQuery(id+"F0.imprint","IMPRINT",EDGE,{"derivedFrom":sQuery(id+"F0.wireOp",EDGE,"E16.bottom")}),-1.0]])]});
            var Q8;
            Q8=makeQuery(id+"F0.imprint","IMPRINT",FACE,{"disambiguationData":[TD([[makeQuery(id+"F0.imprint","IMPRINT",EDGE,{"derivedFrom":sQuery(id+"F0.wireOp",EDGE,"E20.0")}),-1.0]])]});
            var Q9;
            Q9=makeQuery(id+"F0.imprint","IMPRINT",FACE,{"disambiguationData":[TD([[makeQuery(id+"F0.imprint","IMPRINT",EDGE,{"derivedFrom":sQuery(id+"F0.wireOp",EDGE,"E10.bottom")}),-1.0]])]});
            var Q10;
            Q10=makeQuery(id+"F0.imprint","IMPRINT",FACE,{"disambiguationData":[TD([[makeQuery(id+"F0.imprint","IMPRINT",EDGE,{"derivedFrom":sQuery(id+"F0.wireOp",EDGE,"E19.0")}),-1.0]])]});
            var Q11;
            Q11=makeQuery(id+"F0.imprint","IMPRINT",FACE,{"disambiguationData":[TD([[makeQuery(id+"F0.imprint","IMPRINT",EDGE,{"derivedFrom":sQuery(id+"F0.wireOp",EDGE,"E7")}),1.0]])]});
            var Q12;
            Q12=makeQuery(id+"F0.imprint","IMPRINT",FACE,{"disambiguationData":[TD([[makeQuery(id+"F0.imprint","IMPRINT",EDGE,{"derivedFrom":sQuery(id+"F0.wireOp",EDGE,"E8.bottom")}),-1.0]])]});
            var Q13;
            Q13=makeQuery(id+"F0.imprint","IMPRINT",FACE,{"disambiguationData":[TD([[makeQuery(id+"F0.imprint","IMPRINT",EDGE,{"derivedFrom":sQuery(id+"F0.wireOp",EDGE,"E3")}),1.0]])]});
            var Q14;
            Q14=makeQuery(id+"F0.imprint","IMPRINT",FACE,{"disambiguationData":[TD([[makeQuery(id+"F0.imprint","IMPRINT",EDGE,{"derivedFrom":sQuery(id+"F0.wireOp",EDGE,"E18.0")}),-1.0]])]});
            extrude(context, id + "F3", {"entities" : qUnion([Q0, Q1, Q2, Q3, Q4, Q5, Q6, Q7, Q8, Q9, Q10, Q11, Q12, Q13, Q14]), "operationType" : NewBodyOperationType.ADD, "depth" : 15 * mm});
        }
    });
